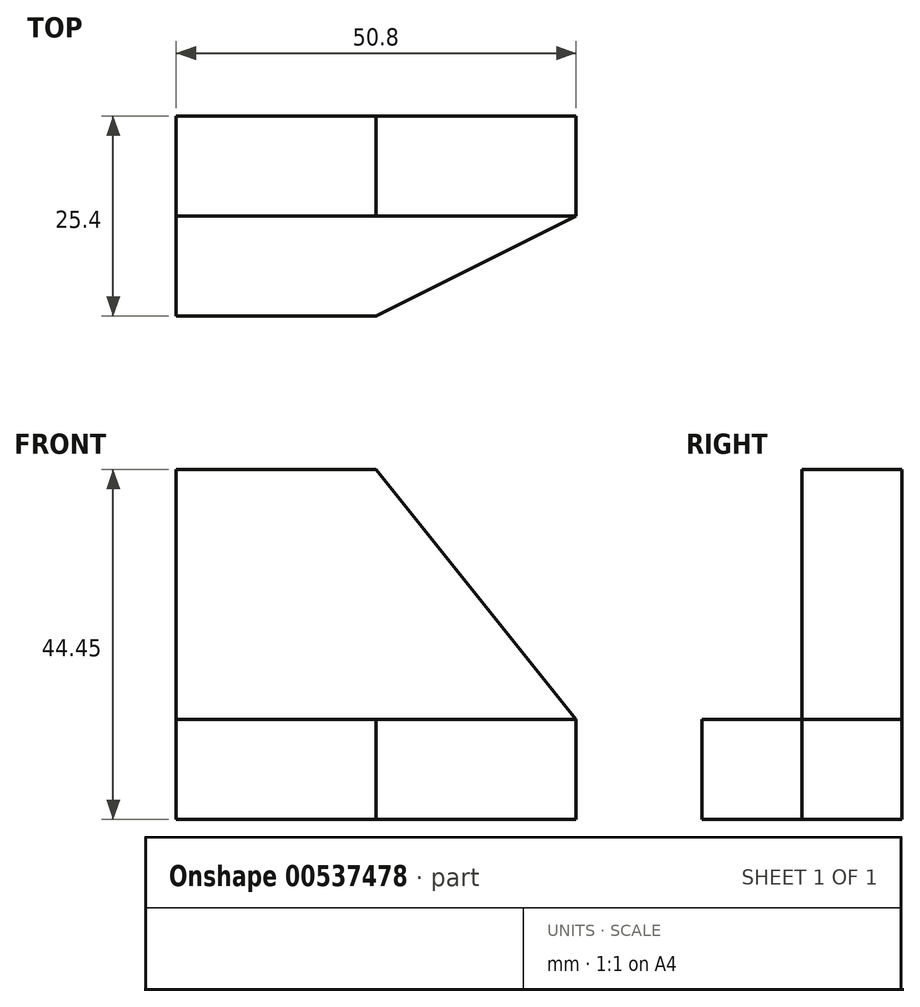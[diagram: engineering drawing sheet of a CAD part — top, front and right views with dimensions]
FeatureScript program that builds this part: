
annotation { "Feature Type Name" : "Feature", "Feature Type Description" : "" }
export const myFeature = defineFeature(function(context is Context, id is Id, definition is map)
    precondition{}
    {
        {
            var Q0;
            Q0=qCreatedBy(makeId("Front.planeOp"),FACE);
            var sketch = newSketch(context, id + "F0", { "sketchPlane" : qUnion([Q0])});
            skLineSegment(sketch, "E0", {"start": v(0, 0) * mm, "end": v(0, 44.45) * mm});
            skLineSegment(sketch, "E1", {"start": v(0, 44.45) * mm, "end": v(25.4, 44.45) * mm});
            skLineSegment(sketch, "E2", {"start": v(25.4, 44.45) * mm, "end": v(50.8, 12.7) * mm});
            skLineSegment(sketch, "E3", {"start": v(50.8, 12.7) * mm, "end": v(50.8, 0) * mm});
            skLineSegment(sketch, "E4", {"start": v(50.8, 0) * mm, "end": v(0, 0) * mm});
            skSolve(sketch);
        }
        {
            var Q0;
            Q0=makeQuery(id+"F0.imprint","IMPRINT",FACE,{"disambiguationData":[TD([[makeQuery(id+"F0.imprint","IMPRINT",EDGE,{"derivedFrom":sQuery(id+"F0.wireOp",EDGE,"E0")}),-1.0]])]});
            extrude(context, id + "F1", {"entities" : qUnion([Q0]), "depth" : 12.7 * mm, "offsetDistance" : 25.4 * mm});
        }
        {
            var Q0;
            Q0=makeQuery(id+"F1.opExtrude","CAP_FACE",FACE,{"disambiguationData":[OSD([sQuery(id+"F0.wireOp",EDGE,"E0"),sQuery(id+"F0.wireOp",EDGE,"E1"),sQuery(id+"F0.wireOp",EDGE,"E2"),sQuery(id+"F0.wireOp",EDGE,"E3"),sQuery(id+"F0.wireOp",EDGE,"E4")])],"isStart":false});
            var sketch = newSketch(context, id + "F2", { "sketchPlane" : qUnion([Q0])});
            skLineSegment(sketch, "E5", {"start": v(50.8, 12.7) * mm, "end": v(0, 12.7) * mm});
            skLineSegment(sketch, "E6", {"start": v(0, 12.7) * mm, "end": v(0, 0) * mm});
            skLineSegment(sketch, "E7", {"start": v(0, 0) * mm, "end": v(50.8, 0) * mm});
            skLineSegment(sketch, "E8", {"start": v(50.8, 0) * mm, "end": v(50.8, 12.7) * mm});
            skSolve(sketch);
        }
        {
            var Q0;
            Q0=makeQuery(id+"F2.imprint","IMPRINT",FACE,{"disambiguationData":[TD([[makeQuery(id+"F2.imprint","IMPRINT",EDGE,{"derivedFrom":sQuery(id+"F2.wireOp",EDGE,"E5")}),1.0]])]});
            extrude(context, id + "F3", {"entities" : qUnion([Q0]), "operationType" : NewBodyOperationType.ADD, "depth" : 12.7 * mm, "offsetDistance" : 25.4 * mm});
        }
        {
            var Q0;
            Q0=makeQuery(id+"F3.opExtrude","SWEPT_FACE",FACE,{"disambiguationData":[OSD([sQuery(id+"F2.wireOp",EDGE,"E5")])]});
            var sketch = newSketch(context, id + "F4", { "sketchPlane" : qUnion([Q0])});
            skLineSegment(sketch, "E9", {"start": v(25.4, -25.4) * mm, "end": v(50.8, -12.7) * mm});
            skLineSegment(sketch, "E10", {"start": v(50.8, -12.7) * mm, "end": v(50.8, -25.4) * mm});
            skLineSegment(sketch, "E11", {"start": v(50.8, -25.4) * mm, "end": v(25.4, -25.4) * mm});
            skSolve(sketch);
        }
        {
            var Q0;
            Q0=makeQuery(id+"F4.imprint","IMPRINT",FACE,{"disambiguationData":[TD([[makeQuery(id+"F4.imprint","IMPRINT",EDGE,{"derivedFrom":sQuery(id+"F4.wireOp",EDGE,"E9")}),-1.0]])]});
            extrude(context, id + "F5", {"entities" : qUnion([Q0]), "operationType" : NewBodyOperationType.REMOVE, "oppositeDirection" : true, "depth" : 25.4 * mm, "offsetDistance" : 25.4 * mm});
        }
    });
